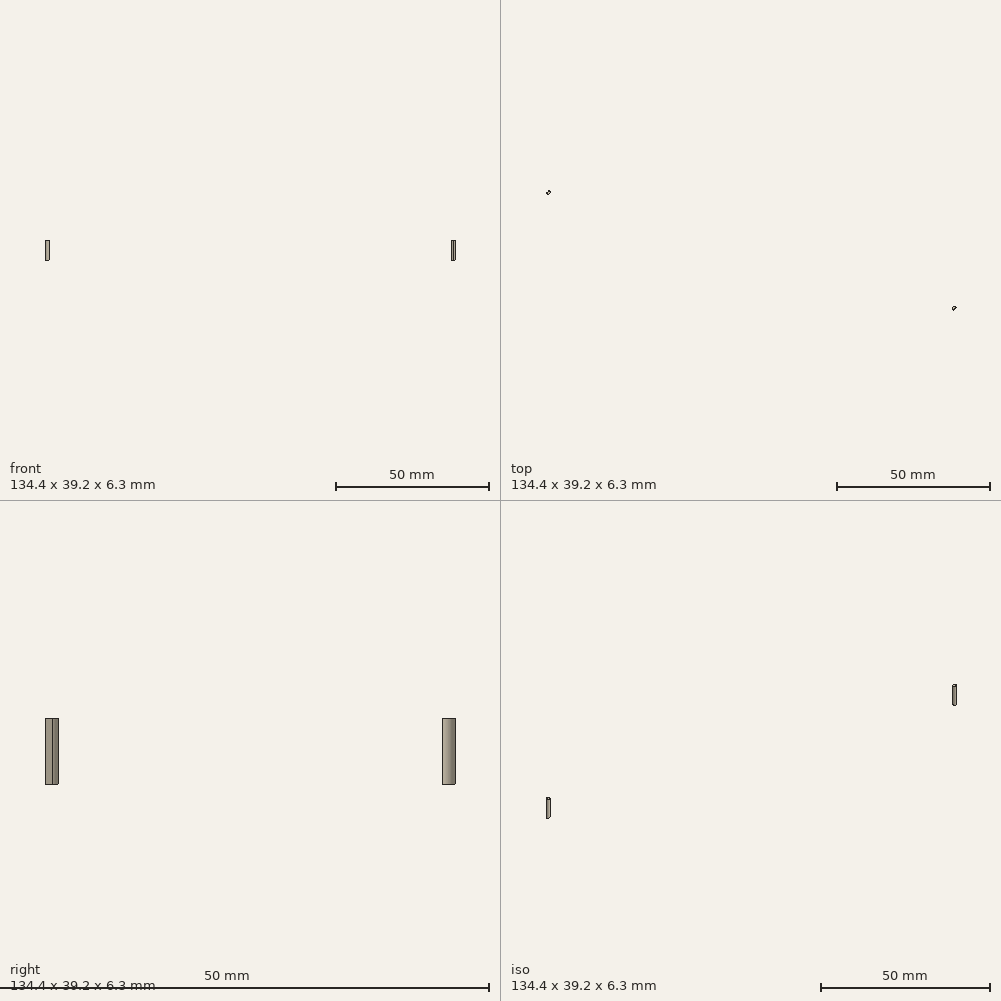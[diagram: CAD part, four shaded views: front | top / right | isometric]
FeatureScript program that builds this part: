
annotation { "Feature Type Name" : "Feature", "Feature Type Description" : "" }
export const myFeature = defineFeature(function(context is Context, id is Id, definition is map)
    precondition{}
    {
        {
            var Q0;
            Q0=qCreatedBy(makeId("Top.planeOp"),FACE);
            var sketch = newSketch(context, id + "F0", { "sketchPlane" : qUnion([Q0])});
            skLineSegment(sketch, "E0.bottom", {"start": v(66.55, -50.8) * mm, "end": v(-66.55, -50.8) * mm});
            skLineSegment(sketch, "E0.top", {"start": v(66.55, 50.8) * mm, "end": v(-66.55, 50.8) * mm});
            skLineSegment(sketch, "E0.left", {"start": v(66.55, -50.8) * mm, "end": v(66.55, 50.8) * mm});
            skLineSegment(sketch, "E0.right", {"start": v(-66.55, -50.8) * mm, "end": v(-66.55, 50.8) * mm});
            skPoint(sketch, "E0.middle", {"position": v(0, 0) * mm});
            skSolve(sketch);
        }
        {
            var Q0;
            Q0=qSketchRegion(id+"F0",true);
            extrude(context, id + "F1", {"entities" : qUnion([Q0]), "depth" : 6.35 * mm, "offsetDistance" : 25.4 * mm});
        }
        {
            var Q0;
            Q0=makeQuery(id+"F1.opExtrude","CAP_FACE",FACE,{"disambiguationData":[OSD([sQuery(id+"F0.wireOp",EDGE,"E0.bottom"),sQuery(id+"F0.wireOp",EDGE,"E0.top"),sQuery(id+"F0.wireOp",EDGE,"E0.left"),sQuery(id+"F0.wireOp",EDGE,"E0.right")])],"isStart":false});
            var sketch = newSketch(context, id + "F2", { "sketchPlane" : qUnion([Q0])});
            skLineSegment(sketch, "E1.bottom", {"start": v(-73.03, 18.99) * mm, "end": v(-66.55, 18.99) * mm});
            skLineSegment(sketch, "E1.top", {"start": v(-73.03, -18.99) * mm, "end": v(-66.55, -18.99) * mm});
            skLineSegment(sketch, "E1.left", {"start": v(-66.55, 18.99) * mm, "end": v(-66.55, -18.99) * mm});
            skLineSegment(sketch, "E1.right", {"start": v(-73.02, 18.99) * mm, "end": v(-73.02, -18.99) * mm});
            skLineSegment(sketch, "E2.bottom", {"start": v(73.02, 18.99) * mm, "end": v(66.55, 18.99) * mm});
            skLineSegment(sketch, "E2.top", {"start": v(73.02, -18.99) * mm, "end": v(66.55, -18.99) * mm});
            skLineSegment(sketch, "E2.left", {"start": v(66.55, 18.99) * mm, "end": v(66.55, -18.99) * mm});
            skLineSegment(sketch, "E2.right", {"start": v(73.03, 18.99) * mm, "end": v(73.03, -18.99) * mm});
            skLineSegment(sketch, "E3", {"start": v(-66.55, 0) * mm, "end": v(66.55, 0) * mm, "construction": true});
            skSolve(sketch);
        }
        {
            var Q0;
            Q0=qSketchRegion(id+"F2",true);
            extrude(context, id + "F3", {"entities" : qUnion([Q0]), "operationType" : NewBodyOperationType.ADD, "oppositeDirection" : true, "depth" : 6.35 * mm, "offsetDistance" : 25.4 * mm});
        }
        {
            var Q0;
            Q0=makeQuery(id+"F1.opExtrude","CAP_FACE",FACE,{"disambiguationData":[OSD([sQuery(id+"F0.wireOp",EDGE,"E0.bottom"),sQuery(id+"F0.wireOp",EDGE,"E0.top"),sQuery(id+"F0.wireOp",EDGE,"E0.left"),sQuery(id+"F0.wireOp",EDGE,"E0.right")])],"isStart":false});
            var sketch = newSketch(context, id + "F4", { "sketchPlane" : qUnion([Q0])});
            skLineSegment(sketch, "E4.bottom", {"start": v(-63.5, 41.28) * mm, "end": v(63.5, 41.28) * mm});
            skLineSegment(sketch, "E4.top", {"start": v(-63.5, 7.94) * mm, "end": v(63.5, 7.94) * mm});
            skLineSegment(sketch, "E4.left", {"start": v(-63.5, 41.28) * mm, "end": v(-63.5, 7.94) * mm});
            skLineSegment(sketch, "E4.right", {"start": v(63.5, 41.28) * mm, "end": v(63.5, 7.94) * mm});
            skLineSegment(sketch, "E5.bottom", {"start": v(-63.5, 4.76) * mm, "end": v(63.5, 4.76) * mm});
            skLineSegment(sketch, "E5.top", {"start": v(-63.5, -46.04) * mm, "end": v(63.5, -46.04) * mm});
            skLineSegment(sketch, "E5.left", {"start": v(-63.5, 4.76) * mm, "end": v(-63.5, -46.04) * mm});
            skLineSegment(sketch, "E5.right", {"start": v(63.5, 4.76) * mm, "end": v(63.5, -46.04) * mm});
            skPoint(sketch, "E6", {"position": v(0, 41.28) * mm});
            skSolve(sketch);
        }
        {
            var Q0;
            Q0 = qSketchRegion(id + "F4", true);
            extrude(context, id + "F5", {"entities" : qUnion([Q0]), "operationType" : NewBodyOperationType.ADD, "depth" : 3.17 * mm, "offsetDistance" : 25.4 * mm});
        }
        {
            var Q0;
            Q0=makeQuery(id+"F3.boolean.opBoolean","MERGE",FACE,{"derivedFrom":[makeQuery(id+"F1.opExtrude","CAP_FACE",FACE,{"disambiguationData":[OSD([sQuery(id+"F0.wireOp",EDGE,"E0.bottom"),sQuery(id+"F0.wireOp",EDGE,"E0.top"),sQuery(id+"F0.wireOp",EDGE,"E0.left"),sQuery(id+"F0.wireOp",EDGE,"E0.right")])],"isStart":true}),makeQuery(id+"F3.opExtrude","CAP_FACE",FACE,{"disambiguationData":[OSD([sQuery(id+"F2.wireOp",EDGE,"E1.bottom"),sQuery(id+"F2.wireOp",EDGE,"E1.top"),sQuery(id+"F2.wireOp",EDGE,"E1.left"),sQuery(id+"F2.wireOp",EDGE,"E1.right")])],"isStart":false}),makeQuery(id+"F3.opExtrude","CAP_FACE",FACE,{"disambiguationData":[OSD([sQuery(id+"F2.wireOp",EDGE,"E2.bottom"),sQuery(id+"F2.wireOp",EDGE,"E2.top"),sQuery(id+"F2.wireOp",EDGE,"E2.left"),sQuery(id+"F2.wireOp",EDGE,"E2.right")])],"isStart":false})]});
            var sketch = newSketch(context, id + "F6", { "sketchPlane" : qUnion([Q0])});
            skArc(sketch, "E7", {"start": v(-67.18, 18.99) * mm, "mid": v(-66.1, 18.54) * mm, "end": v(-66.55, 19.62) * mm});
            skArc(sketch, "E8", {"start": v(-67.18, -18.99) * mm, "mid": v(-66.1, -18.54) * mm, "end": v(-66.55, -19.62) * mm});
            skArc(sketch, "E9", {"start": v(67.18, -18.99) * mm, "mid": v(66.1, -18.54) * mm, "end": v(66.55, -19.62) * mm});
            skArc(sketch, "E10", {"start": v(67.18, 18.99) * mm, "mid": v(66.1, 18.54) * mm, "end": v(66.55, 19.62) * mm});
            skLineSegment(sketch, "E11", {"start": v(66.55, 18.99) * mm, "end": v(66.55, 19.62) * mm});
            skLineSegment(sketch, "E12", {"start": v(66.55, 18.99) * mm, "end": v(67.18, 18.99) * mm});
            skLineSegment(sketch, "E13", {"start": v(66.55, -18.99) * mm, "end": v(67.18, -18.99) * mm});
            skLineSegment(sketch, "E14", {"start": v(66.55, -18.99) * mm, "end": v(66.55, -19.62) * mm});
            skLineSegment(sketch, "E15", {"start": v(-66.55, -18.99) * mm, "end": v(-66.55, -19.62) * mm});
            skLineSegment(sketch, "E16", {"start": v(-66.55, 18.99) * mm, "end": v(-66.55, 19.62) * mm});
            skLineSegment(sketch, "E17", {"start": v(-66.55, 18.99) * mm, "end": v(-67.18, 18.99) * mm});
            skLineSegment(sketch, "E18", {"start": v(-66.55, -18.99) * mm, "end": v(-67.18, -18.99) * mm});
            skSolve(sketch);
        }
        {
            var Q0;
            Q0=makeQuery(id+"F6.imprint","IMPRINT",FACE,{"disambiguationData":[TD([[makeQuery(id+"F6.imprint","IMPRINT",EDGE,{"derivedFrom":sQuery(id+"F6.wireOp",EDGE,"E8")}),-1.0]])]});
            var Q1;
            Q1=makeQuery(id+"F6.imprint","IMPRINT",FACE,{"disambiguationData":[TD([[makeQuery(id+"F6.imprint","IMPRINT",EDGE,{"derivedFrom":sQuery(id+"F6.wireOp",EDGE,"E7")}),1.0]])]});
            var Q2;
            Q2=makeQuery(id+"F6.imprint","IMPRINT",FACE,{"disambiguationData":[TD([[makeQuery(id+"F6.imprint","IMPRINT",EDGE,{"derivedFrom":sQuery(id+"F6.wireOp",EDGE,"E9")}),1.0]])]});
            var Q3;
            Q3=makeQuery(id+"F6.imprint","IMPRINT",FACE,{"disambiguationData":[TD([[makeQuery(id+"F6.imprint","IMPRINT",EDGE,{"derivedFrom":sQuery(id+"F6.wireOp",EDGE,"E10")}),-1.0]])]});
            extrude(context, id + "F7", {"entities" : qUnion([Q0, Q1, Q2, Q3]), "operationType" : NewBodyOperationType.REMOVE, "endBound" : BoundingType.THROUGH_ALL, "oppositeDirection" : true, "depth" : 25.4 * mm, "offsetDistance" : 25.4 * mm});
        }
    });
